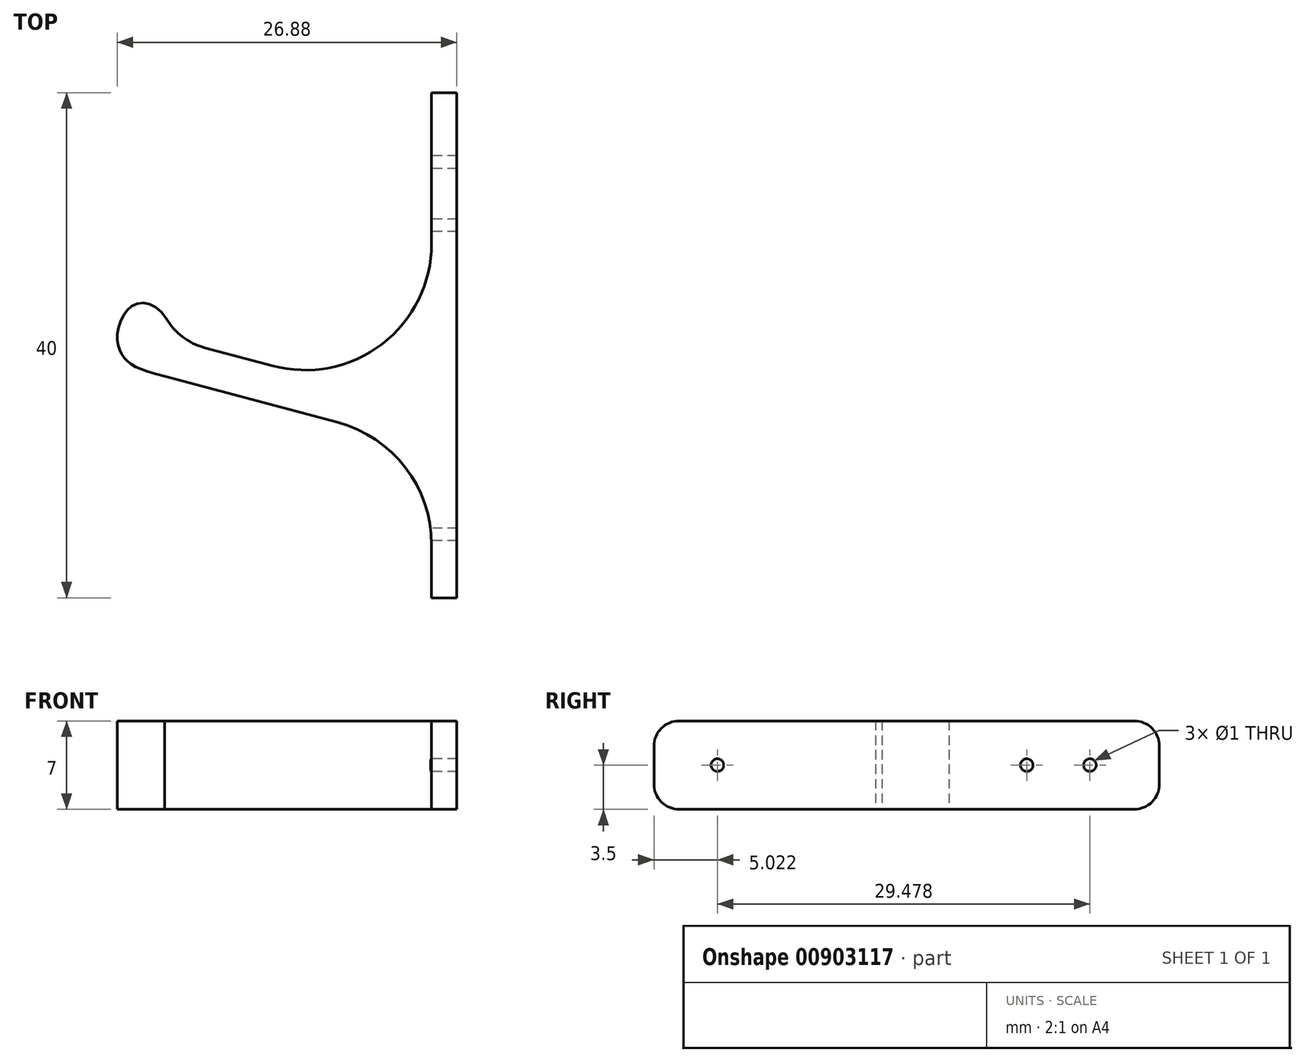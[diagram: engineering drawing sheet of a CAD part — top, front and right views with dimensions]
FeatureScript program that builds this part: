
annotation { "Feature Type Name" : "Feature", "Feature Type Description" : "" }
export const myFeature = defineFeature(function(context is Context, id is Id, definition is map)
    precondition{}
    {
        {
            var Q0;
            Q0=qCreatedBy(makeId("Top.planeOp"),FACE);
            var sketch = newSketch(context, id + "F0", { "sketchPlane" : qUnion([Q0])});
            skLineSegment(sketch, "E0", {"start": v(0, 25) * mm, "end": v(0, 13.03) * mm});
            skLineSegment(sketch, "E1", {"start": v(-12.59, 3.37) * mm, "end": v(-17.97, 4.81) * mm});
            skLineSegment(sketch, "E2.0", {"start": v(-7.41, -1.12) * mm, "end": v(-21.12, 2.55) * mm});
            skLineSegment(sketch, "E3.0", {"start": v(2, 25) * mm, "end": v(2, -15) * mm});
            skLineSegment(sketch, "E4", {"start": v(0, 25) * mm, "end": v(2, 25) * mm});
            skLineSegment(sketch, "E5", {"start": v(0, -15) * mm, "end": v(2, -15) * mm});
            skFitSpline(sketch, "E6", {"points": [v(-20.66, 5.53) * mm, v(-23.14, 8.34) * mm, v(-24.86, 5.9) * mm, v(-24.24, 3.92) * mm, v(-21.12, 2.55) * mm], "startDerivative": vector(1.96, 19.12) * mm, "endDerivative": vector(20.7, -4.96) * mm});
            skLineSegment(sketch, "E7.trimOffspring", {"start": v(0, -10.78) * mm, "end": v(0, -15) * mm});
            skPoint(sketch, "E8.visualSharp", {"position": v(0, 0) * mm});
            skArc(sketch, "E8.filletArc", {"start": v(-12.59, 3.37) * mm, "mid": v(-3.91, 5.1) * mm, "end": v(0, 13.03) * mm});
            skPoint(sketch, "E9.visualSharp", {"position": v(0, -3.1) * mm});
            skArc(sketch, "E9.filletArc", {"start": v(0, -10.78) * mm, "mid": v(-2.07, -4.7) * mm, "end": v(-7.41, -1.12) * mm});
            skArc(sketch, "E10.filletArc", {"start": v(-21, 7.13) * mm, "mid": v(-19.7, 5.67) * mm, "end": v(-17.97, 4.81) * mm});
            skSolve(sketch);
        }
        {
            var Q0;
            Q0=makeQuery(id+"F0.imprint","IMPRINT",FACE,{"disambiguationData":[TD([[makeQuery(id+"F0.imprint","IMPRINT",EDGE,{"derivedFrom":sQuery(id+"F0.wireOp",EDGE,"E0")}),1.0]])]});
            extrude(context, id + "F1", {"entities" : qUnion([Q0]), "depth" : 7 * mm, "offsetDistance" : 25 * mm});
        }
        {
            var Q0;
            Q0=makeQuery(id+"F1.opExtrude","CAP_EDGE",EDGE,{"disambiguationData":[OSD([sQuery(id+"F0.wireOp",EDGE,"E4")])],"isStart":true});
            var Q1;
            Q1=makeQuery(id+"F1.opExtrude","CAP_EDGE",EDGE,{"disambiguationData":[OSD([sQuery(id+"F0.wireOp",EDGE,"E4")])],"isStart":false});
            var Q2;
            Q2=makeQuery(id+"F1.opExtrude","CAP_EDGE",EDGE,{"disambiguationData":[OSD([sQuery(id+"F0.wireOp",EDGE,"E5")])],"isStart":true});
            var Q3;
            Q3=makeQuery(id+"F1.opExtrude","CAP_EDGE",EDGE,{"disambiguationData":[OSD([sQuery(id+"F0.wireOp",EDGE,"E5")])],"isStart":false});
            fillet(context, id + "F2", {"entities" : qUnion([Q0, Q1, Q2, Q3]), "radius" : 2 * mm, "tangentPropagation" : true, "allowEdgeOverflow" : false});
        }
        {
            var Q0;
            Q0=makeQuery(id+"F1.opExtrude","SWEPT_FACE",FACE,{"disambiguationData":[OSD([sQuery(id+"F0.wireOp",EDGE,"E0")])]});
            var sketch = newSketch(context, id + "F3", { "sketchPlane" : qUnion([Q0])});
            skLineSegment(sketch, "E11", {"start": v(-25, 3.5) * mm, "end": v(14.98, 3.5) * mm, "construction": true});
            skCircle(sketch, "E12", {"center": v(-19.5, 3.5) * mm, "radius": 0.5 * mm});
            skPoint(sketch, "E12.centerSnap0", {"position": v(-18.02, 0) * mm});
            skCircle(sketch, "E13", {"center": v(-14.5, 3.5) * mm, "radius": 0.5 * mm});
            skCircle(sketch, "E14", {"center": v(9.98, 3.5) * mm, "radius": 0.5 * mm});
            skSolve(sketch);
        }
        {
            var Q0;
            Q0 = qSketchRegion(id + "F3", true);
            extrude(context, id + "F4", {"entities" : qUnion([Q0]), "operationType" : NewBodyOperationType.REMOVE, "endBound" : BoundingType.THROUGH_ALL, "oppositeDirection" : true, "depth" : 25 * mm, "offsetDistance" : 25 * mm, "hasSecondDirection" : true, "secondDirectionBound" : SecondDirectionBoundingType.THROUGH_ALL, "secondDirectionOppositeDirection" : false, "secondDirectionDepth" : 25 * mm});
        }
    });
